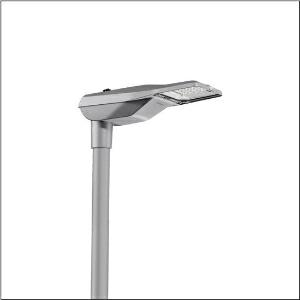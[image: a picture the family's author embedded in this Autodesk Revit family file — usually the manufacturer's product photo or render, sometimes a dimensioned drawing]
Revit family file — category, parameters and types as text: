
# Revit family: streetlight_sl_21_iq_micro___st1_0a_5xe1d31v08db_4967
name_source: partatom
category: Lighting Fixtures
units: mm (PartAtom-declared; Revit-internal decimal feet)

## family parameters
Cut with Voids When Loaded = No
Host = Face
Light Source = No
Part Type = Normal
Room Calculation Point = No
Round Connector Dimension = Use Diameter
Shared = No

## types (1)
- --- (1 x LED, 5110 lm, 39.1 W, 3000K)
    Apparent Load = 39 VA
    CIE Flux Codes = 37 72 97 100 100
    Color Rendering = 70
    Color Temperature = 3000K
    Default Elevation = 1800 mm
    Description = Streetlight SL 21 iQ micro, mast luminaire, primary light control with lens, of PMMA, primary optical cover: cover, of toughened safety glass, transparent, light distribution: ST1.0a, light emission: direct distribution, primary light characteristic: asymmetric, installation type: post-top, side-entry, LED, High Power LED, rated luminous flux: 5.110lm, luminous efficacy: 131lm/W, light colour: 730, colour temperature: 3000K, control: presetting dimming logarithmic, Street-Remote, Auto-Match, Temp-Guard, Lumen-Switch, Night-Set, Smart-Wire, Light-Fading, Desk-Remote (wireless, voltage-free reading and setting of iQ features in the workshop via application-optimized NFC function/RFID function), optimised constant luminous flux control (CLO 2.0), mains connection: 220..240V, AC, 50/60Hz, start of lifetime: 39W, end of service life: 41W, reduction: 17W, luminaire housing, of diecast aluminium, powder-coated, Siteco® metallic grey (DB 702S), corrosivity category C5 mid according to DIN EN ISO 12944, please order mast flange separately, inclination adjustable: 0°, 5°, 10°, 15°, sealing non-destructively replaceable, multi-level sealing system, length: 528mm, width: 235mm, height: 110mm, mast flange for spigot size: 42mm (side-entry): 5XC10008XM4, 60/48mm (side-entry/post-top): 5XC10108XM2, 76/60mm (side-entry/post-top): 5XC10108XM1, Smart Interface above, protection rating (complete): IP66, insulation class (complete): insulation class II (safety insulation), certification: CE, ENEC, ENEC+, VDE, impact resistance: IK09, permissible operating ambient temperature for outdoor applications: -40..+50°C, standard-compliant lighting for roads and squares, packaging unit: 1 piece

Light Distribution: ST1.0a
    Height = 110 mm
    Lamp = 1 x LED
    Lamp Light Flux = 5110 lm
    Lamp Power = 39.1 W
    Lamp count = 1
    Length = 528 mm
    Luminous efficacy = 131 lm/W
    Manufacturer = Siteco
    ModVariant = No
    Model = 5XE1D31V08DB
    Number of Poles = 1
    OnlyDefault = Yes
    Power Factor = 1
    Product Name = Streetlight SL 21 iQ micro | ST1.0a
    Product group = mast luminaire | pylon top
    ProductGroupID = 6100
    Protection Class = Protection class II
    Protection Degree = IP 66
    RLX_Detail_Level = 1
    RLX_Emergency_Light_Flux = 0 lm
    RLX_Emergency_Type = 0
    RLX_Emergency_Type_DB = No
    RlxData = <blob elided: 98337 chars, md5=9bb9275e>
    Socket = socket
    Standby Power = 0 W
    System Light Flux = 5110 lm
    System Power = 39 W
    Type Comments = factory setting: luminous flux: 100 % | dim-lin: 254 | 765 mA
    Type Image = l_1277292.jpg
    URL = http://relux.com
    VarID = @adj_063843
    Voltage = 0 V
    Weight = 0.00 kg
    Width = 235 mm

## geometry (parser evidence)
native form markers: Blend x4, Sweep x9
no freeform markers — native parametric forms only
